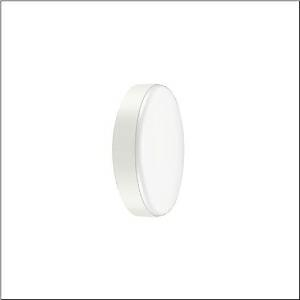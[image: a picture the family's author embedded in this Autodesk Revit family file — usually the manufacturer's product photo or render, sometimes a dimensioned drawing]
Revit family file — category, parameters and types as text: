
# Revit family: round_31_51wc10da32as
name_source: partatom
category: Lighting Fixtures
units: mm (PartAtom-declared; Revit-internal decimal feet)

## family parameters
Cut with Voids When Loaded = No
Host = Face
Light Source = No
Part Type = Normal
Room Calculation Point = No
Round Connector Dimension = Use Diameter
Shared = No

## types (1)
- Round 31 (1 x LED, 2450 lm, 20.4 W, 3000K)
    Apparent Load = 20 VA
    CIE Flux Codes = 44 75 94 94 100
    Color Rendering = 80
    Color Temperature = 3000K
    Default Elevation = 1800 mm
    Description = Round 31, wall and ceiling luminaire, primary optical cover: cover, of PC, opal, light emission: direct distribution, primary light characteristic: symmetric, installation type: surface-mounted, LED, rated luminous flux: 2.450lm, luminous efficacy: 120lm/W, light colour: 830, colour temperature: 3000K, control gear: DALI 2, with terminal, 5-pole, max. 2.5mm², mains connection: 220..240V, AC, 50/60Hz, rated input power: 20.5W, luminaire housing, of PC, traffic white (RAL 9016), diameter: 350mm, brightness and presence sensor, HF sensor, protection rating (complete): IP65, insulation class (complete): insulation class II (safety insulation), certification: CE, impact resistance: IK10, permissible operating ambient temperature: -20..+40°C, permissible storage temperature: -20..+60°C, packaging unit: 1 piece
    Height = 97 mm
    Lamp = 1 x LED
    Lamp Light Flux = 2450 lm
    Lamp Power = 20.4 W
    Lamp count = 1
    Length = 350 mm
    Luminous efficacy = 120 lm/W
    Manufacturer = Siteco
    ModVariant = No
    Model = 51WC10DA32AS
    Mounting Place = Ceiling
    Mounting Type = Surface mounted
    Number of Poles = 1
    OnlyDefault = Yes
    Power Factor = 1
    Product Name = Round 31
    Product group = wall and ceiling luminaire
    ProductGroupID = 304
    Protection Class = Protection class II
    Protection Degree = IP 65
    RLX_Detail_Level = 1
    RLX_Emergency_Light_Flux = 0 lm
    RLX_Emergency_Type = 0
    RLX_Emergency_Type_DB = No
    RlxData = <blob elided: 29617 chars, md5=c7d281ac>
    Socket = socket
    Standby Power = 0 W
    System Light Flux = 2450 lm
    System Power = 20 W
    Type Comments = Product without accessories
    Type Image = l_1007027.jpg
    URL = http://relux.com
    VarID = ---
    Voltage = 0 V
    Weight = 0.00 kg
    Width = 0 mm  [stored 0 ft]

note: [stored X ft] marks values corroborated as IEEE doubles in the binary element streams (Revit-internal decimal feet)

## geometry (parser evidence)
native form markers: Blend x4, Sweep x12
no freeform markers — native parametric forms only
